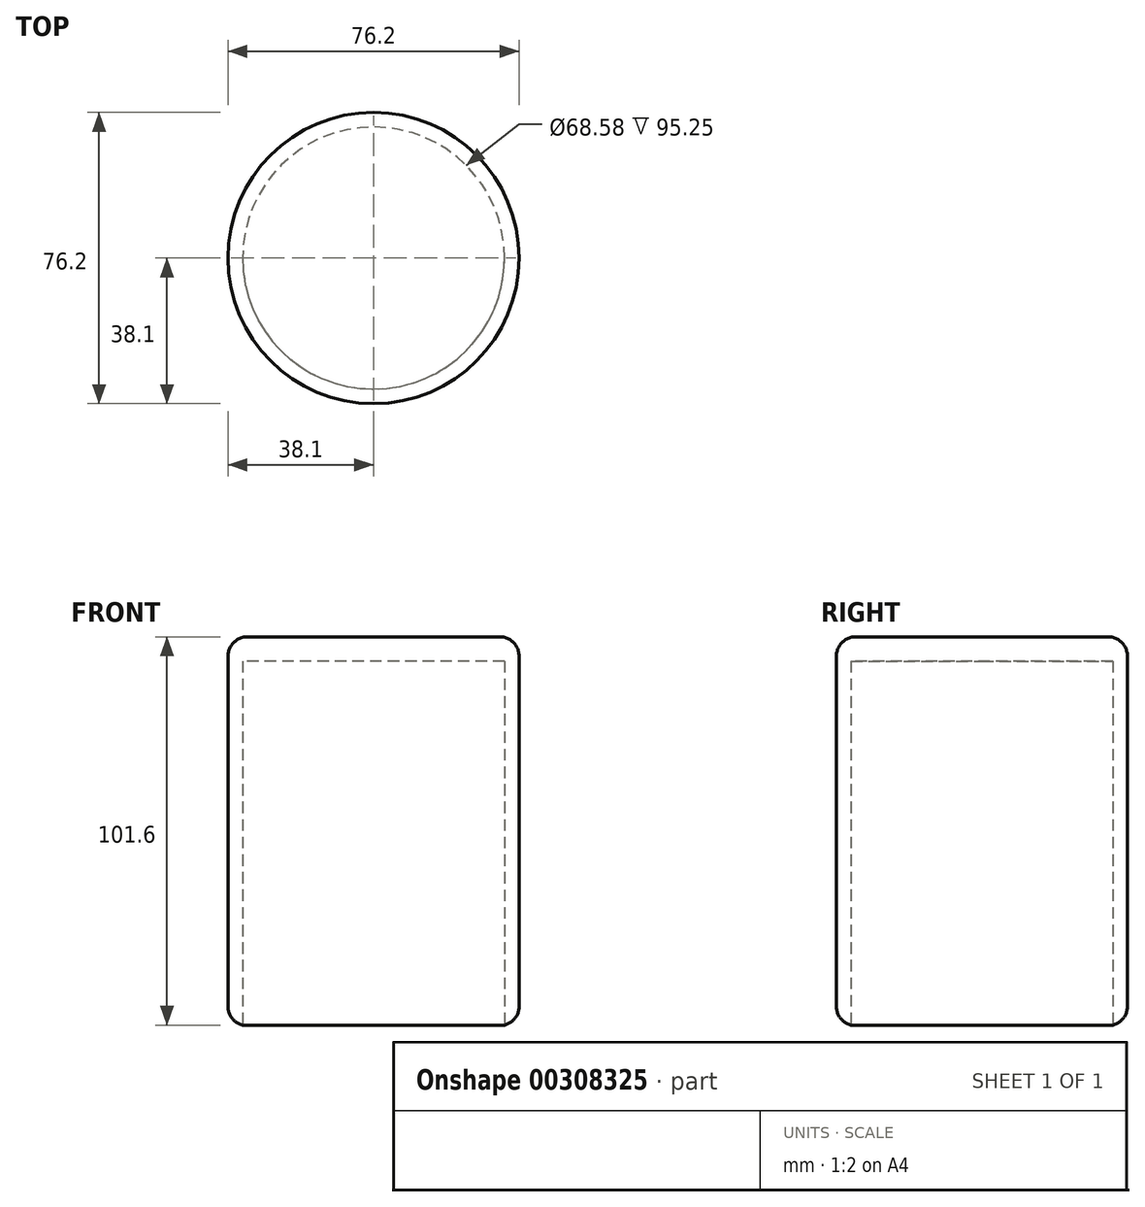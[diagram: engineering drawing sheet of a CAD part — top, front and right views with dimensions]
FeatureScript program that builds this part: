
annotation { "Feature Type Name" : "Feature", "Feature Type Description" : "" }
export const myFeature = defineFeature(function(context is Context, id is Id, definition is map)
    precondition{}
    {
        {
            var Q0;
            Q0=qCreatedBy(makeId("Top.planeOp"),FACE);
            var sketch = newSketch(context, id + "F0", { "sketchPlane" : qUnion([Q0])});
            skCircle(sketch, "E0", {"center": v(0, 0) * mm, "radius": 38.1 * mm});
            skSolve(sketch);
        }
        {
            var Q0;
            Q0=makeQuery(id+"F0.imprint","IMPRINT",FACE,{"disambiguationData":[TD([[makeQuery(id+"F0.imprint","IMPRINT",EDGE,{"derivedFrom":sQuery(id+"F0.wireOp",EDGE,"E0")}),1.0]])]});
            extrude(context, id + "F1", {"entities" : qUnion([Q0]), "depth" : 101.6 * mm});
        }
        {
            var Q0;
            Q0=qCreatedBy(makeId("Top.planeOp"),FACE);
            var sketch = newSketch(context, id + "F2", { "sketchPlane" : qUnion([Q0])});
            skCircle(sketch, "E1", {"center": v(0, 0) * mm, "radius": 34.3 * mm});
            skSolve(sketch);
        }
        {
            var Q0;
            Q0=makeQuery(id+"F2.imprint","IMPRINT",FACE,{"disambiguationData":[TD([[makeQuery(id+"F2.imprint","IMPRINT",EDGE,{"derivedFrom":sQuery(id+"F2.wireOp",EDGE,"E1")}),1.0]])]});
            extrude(context, id + "F3", {"entities" : qUnion([Q0]), "operationType" : NewBodyOperationType.REMOVE, "depth" : 95.25 * mm});
        }
        {
            var Q0;
            Q0=makeQuery(id+"F1.opExtrude","CAP_EDGE",EDGE,{"disambiguationData":[OSD([sQuery(id+"F0.wireOp",EDGE,"E0")])],"isStart":true});
            var Q1;
            Q1=makeQuery(id+"F1.opExtrude","CAP_EDGE",EDGE,{"disambiguationData":[OSD([sQuery(id+"F0.wireOp",EDGE,"E0")])],"isStart":false});
            fillet(context, id + "F4", {"entities" : qUnion([Q0, Q1]), "radius" : 5.08 * mm, "tangentPropagation" : true, "allowEdgeOverflow" : false});
        }
    });
